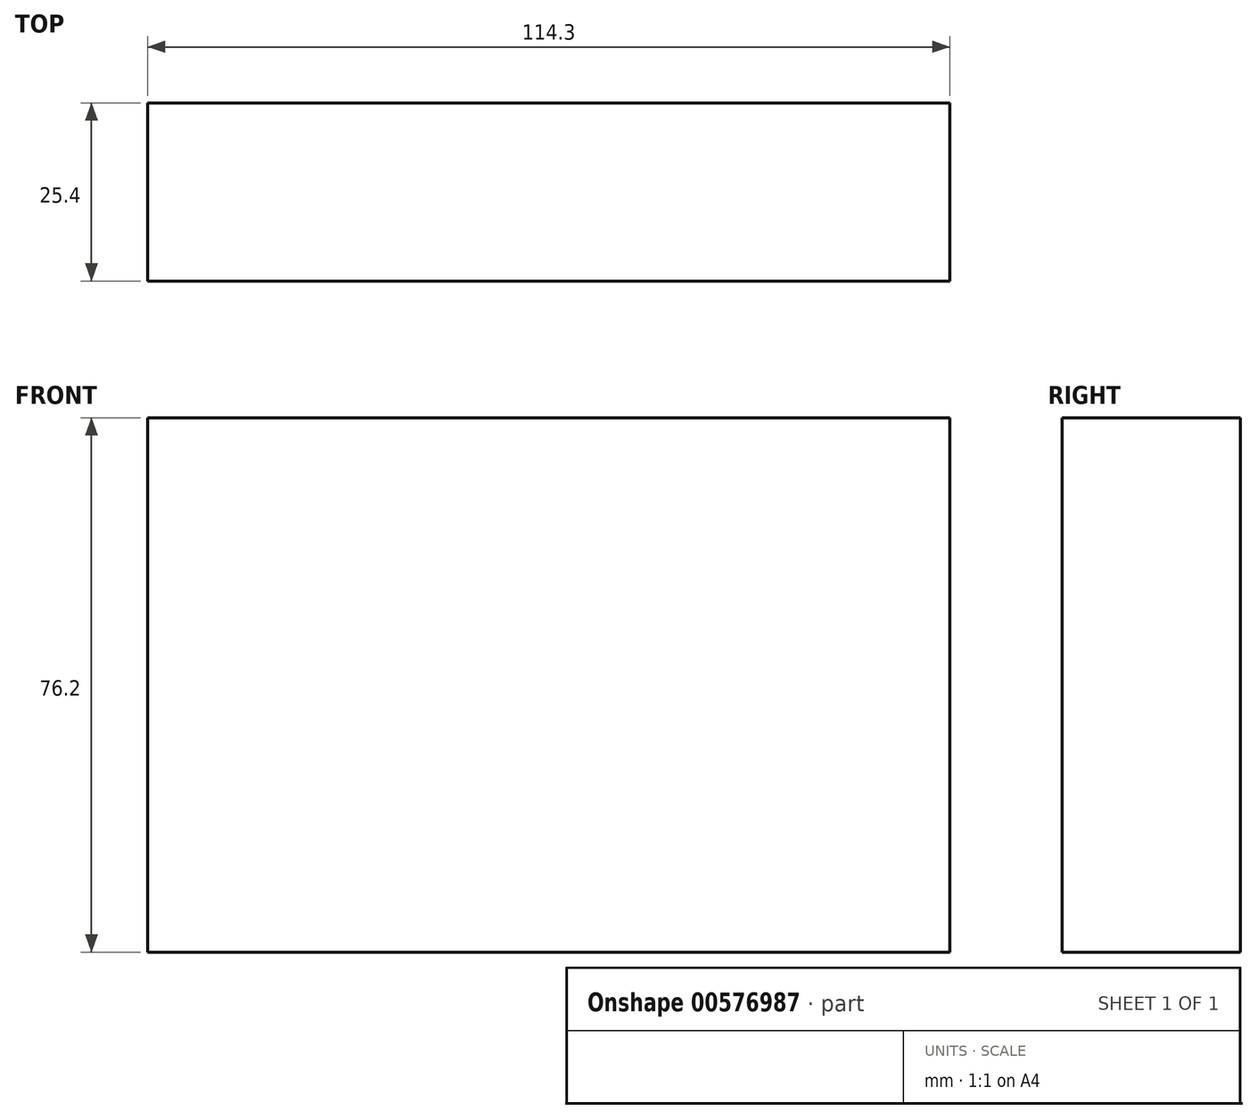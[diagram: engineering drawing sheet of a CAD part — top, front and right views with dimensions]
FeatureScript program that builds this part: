
annotation { "Feature Type Name" : "Feature", "Feature Type Description" : "" }
export const myFeature = defineFeature(function(context is Context, id is Id, definition is map)
    precondition{}
    {
        {
            var Q0;
            Q0=qCreatedBy(makeId("Front.planeOp"),FACE);
            var sketch = newSketch(context, id + "F0", { "sketchPlane" : qUnion([Q0])});
            skLineSegment(sketch, "E0.bottom", {"start": v(-57.15, 38.1) * mm, "end": v(57.15, 38.1) * mm});
            skLineSegment(sketch, "E0.top", {"start": v(-57.15, -38.1) * mm, "end": v(57.15, -38.1) * mm});
            skLineSegment(sketch, "E0.left", {"start": v(-57.15, 38.1) * mm, "end": v(-57.15, -38.1) * mm});
            skLineSegment(sketch, "E0.right", {"start": v(57.15, 38.1) * mm, "end": v(57.15, -38.1) * mm});
            skPoint(sketch, "E0.middle", {"position": v(0, 0) * mm});
            skSolve(sketch);
        }
        {
            var Q0;
            Q0 = qSketchRegion(id + "F0", true);
            extrude(context, id + "F1", {"entities" : qUnion([Q0]), "depth" : 25.4 * mm, "offsetDistance" : 25.4 * mm});
        }
    });
